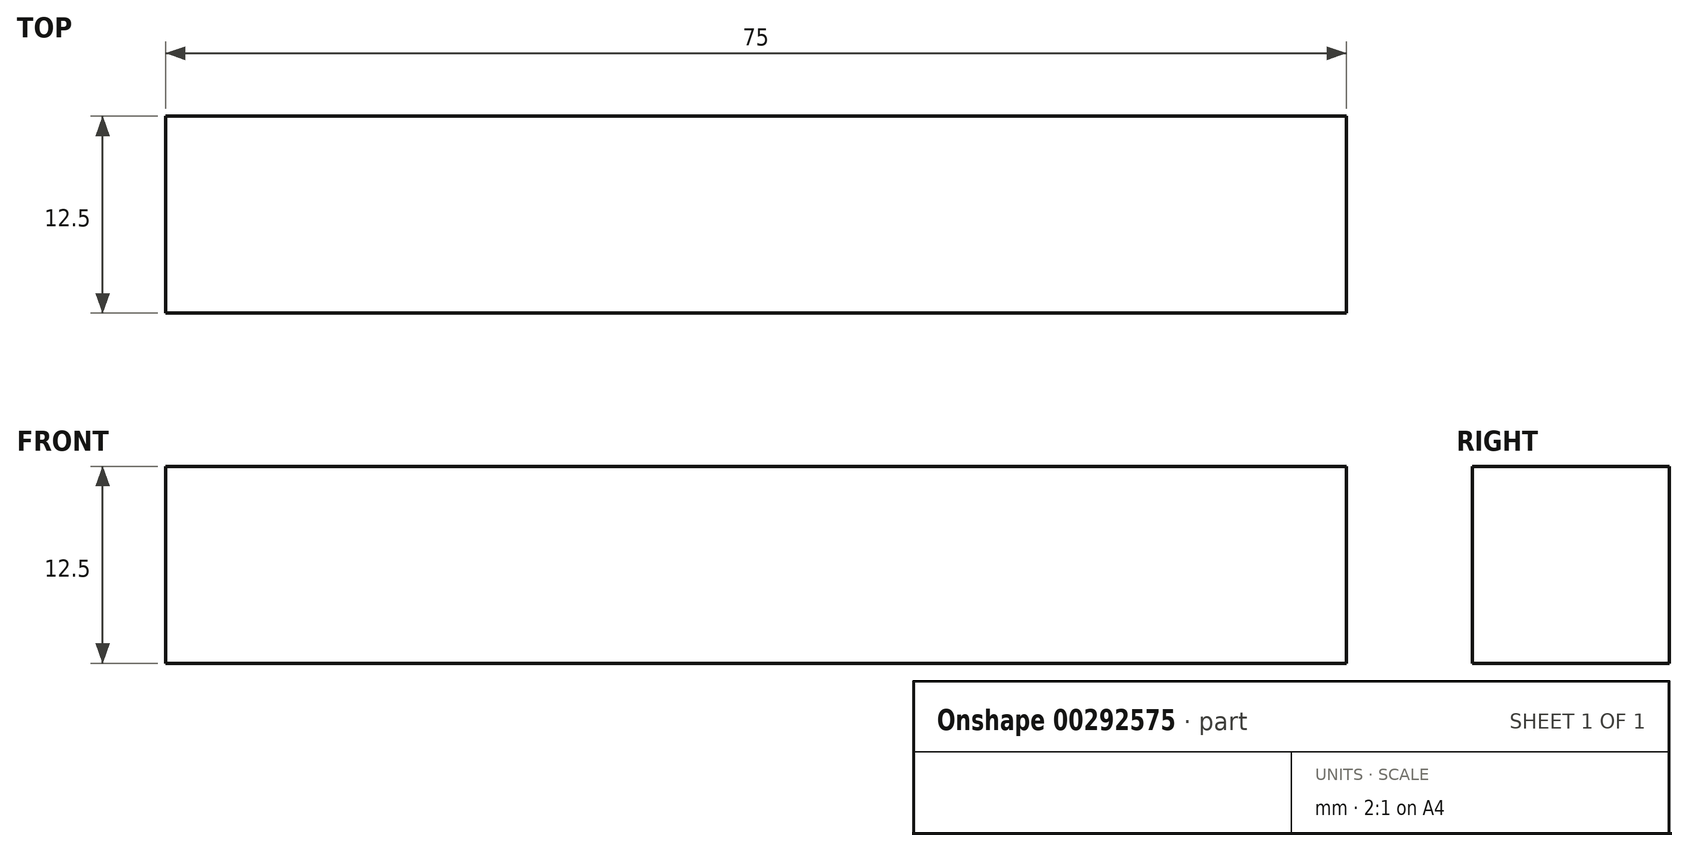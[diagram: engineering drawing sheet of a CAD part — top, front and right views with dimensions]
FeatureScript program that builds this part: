
annotation { "Feature Type Name" : "Feature", "Feature Type Description" : "" }
export const myFeature = defineFeature(function(context is Context, id is Id, definition is map)
    precondition{}
    {
        {
            var Q0;
            Q0=qCreatedBy(makeId("Front.planeOp"),FACE);
            var sketch = newSketch(context, id + "F0", { "sketchPlane" : qUnion([Q0])});
            skLineSegment(sketch, "E0", {"start": v(-31.43, 0.92) * mm, "end": v(43.57, 0.92) * mm});
            skLineSegment(sketch, "E1", {"start": v(43.57, 0.92) * mm, "end": v(43.57, -11.58) * mm});
            skLineSegment(sketch, "E2", {"start": v(43.57, -11.58) * mm, "end": v(-31.43, -11.58) * mm});
            skLineSegment(sketch, "E3", {"start": v(-31.43, -11.58) * mm, "end": v(-31.43, 0.92) * mm});
            skSolve(sketch);
        }
        {
            var Q0;
            Q0 = qSketchRegion(id + "F0", true);
            extrude(context, id + "F1", {"entities" : qUnion([Q0]), "depth" : 12.5 * mm});
        }
    });
